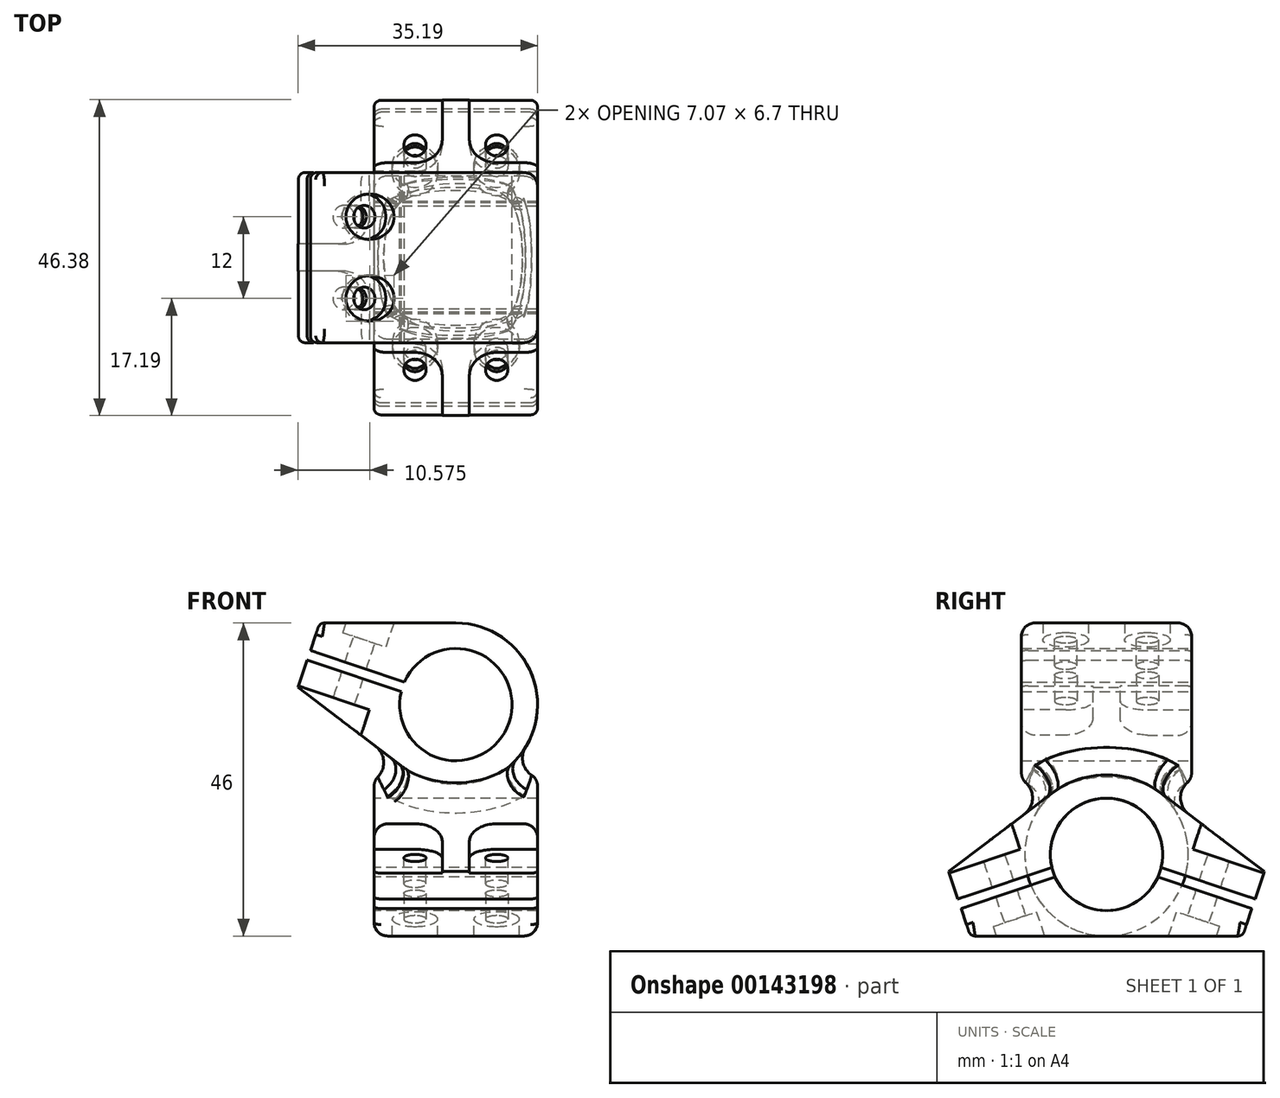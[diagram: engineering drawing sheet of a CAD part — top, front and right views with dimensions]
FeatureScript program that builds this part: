
annotation { "Feature Type Name" : "Feature", "Feature Type Description" : "" }
export const myFeature = defineFeature(function(context is Context, id is Id, definition is map)
    precondition{}
    {
        {
            var Q0;
            Q0=qCreatedBy(makeId("Front.planeOp"),FACE);
            var sketch = newSketch(context, id + "F0", { "sketchPlane" : qUnion([Q0])});
            skCircle(sketch, "E0", {"center": v(0, 11) * mm, "radius": 8.25 * mm});
            skCircle(sketch, "E1", {"center": v(0, 11) * mm, "radius": 12 * mm});
            skSolve(sketch);
        }
        {
            var Q0;
            Q0=qCreatedBy(makeId("Right.planeOp"),FACE);
            var sketch = newSketch(context, id + "F1", { "sketchPlane" : qUnion([Q0])});
            skCircle(sketch, "E2", {"center": v(0, -11) * mm, "radius": 8.25 * mm});
            skCircle(sketch, "E3", {"center": v(0, -11) * mm, "radius": 12 * mm});
            skSolve(sketch);
        }
        {
            var Q0;
            Q0=qSketchRegion(id+"F1",true);
            extrude(context, id + "F2", {"entities" : qUnion([Q0]), "endBound" : BoundingType.SYMMETRIC, "depth" : 24 * mm});
        }
        {
            var Q0;
            Q0=qSketchRegion(id+"F0",true);
            extrude(context, id + "F3", {"entities" : qUnion([Q0]), "operationType" : NewBodyOperationType.ADD, "endBound" : BoundingType.SYMMETRIC, "depth" : 25 * mm});
        }
        {
            var Q0;
            Q0=makeQuery(id+"F3.opExtrude","CAP_FACE",FACE,{"disambiguationData":[OSD([sQuery(id+"F0.wireOp",EDGE,"E0"),sQuery(id+"F0.wireOp",EDGE,"E1")])],"isStart":true});
            var sketch = newSketch(context, id + "F4", { "sketchPlane" : qUnion([Q0])});
            skLineSegment(sketch, "E4", {"start": v(0, 23) * mm, "end": v(20, 23) * mm});
            skLineSegment(sketch, "E5", {"start": v(7.25, 1.44) * mm, "end": v(23.19, 13.52) * mm});
            skLineSegment(sketch, "E6", {"start": v(20, 23) * mm, "end": v(23.19, 13.52) * mm});
            skLineSegment(sketch, "E7", {"start": v(21.6, 18.26) * mm, "end": v(-4.56, 9.47) * mm, "construction": true});
            skSolve(sketch);
        }
        {
            var Q0;
            {var subQ2=sQuery(id+"F4.wireOp",EDGE,"E4");Q0=makeQuery(id+"F4.imprint","IMPRINT",FACE,{"disambiguationData":[TD([[makeQuery(id+"F4.imprint","IMPRINT",EDGE,{"derivedFrom":subQ2}),-1.0]])]});}
            var Q1;
            Q1=makeQuery(id+"F3.opExtrude","CAP_FACE",FACE,{"disambiguationData":[OSD([sQuery(id+"F0.wireOp",EDGE,"E0"),sQuery(id+"F0.wireOp",EDGE,"E1")])],"isStart":false});
            extrude(context, id + "F5", {"entities" : qUnion([Q0]), "operationType" : NewBodyOperationType.ADD, "endBound" : BoundingType.UP_TO_SURFACE, "oppositeDirection" : true, "endBoundEntityFace" : qUnion([Q1]), "depth" : 25 * mm});
        }
        {
            var Q0;
            Q0=makeQuery(id+"F2.opExtrude","CAP_FACE",FACE,{"disambiguationData":[OSD([sQuery(id+"F1.wireOp",EDGE,"E2"),sQuery(id+"F1.wireOp",EDGE,"E3")])],"isStart":false});
            var sketch = newSketch(context, id + "F6", { "sketchPlane" : qUnion([Q0])});
            skLineSegment(sketch, "E8", {"start": v(0, -23) * mm, "end": v(-20, -23) * mm});
            skLineSegment(sketch, "E9", {"start": v(-7.25, -1.44) * mm, "end": v(-23.19, -13.52) * mm});
            skLineSegment(sketch, "E10", {"start": v(-20, -23) * mm, "end": v(-23.19, -13.52) * mm});
            skSolve(sketch);
        }
        {
            var Q0;
            {var subQ2=sQuery(id+"F6.wireOp",EDGE,"E8");Q0=makeQuery(id+"F6.imprint","IMPRINT",FACE,{"disambiguationData":[TD([[makeQuery(id+"F6.imprint","IMPRINT",EDGE,{"derivedFrom":subQ2}),-1.0]])]});}
            var Q1;
            Q1=makeQuery(id+"F2.opExtrude","CAP_FACE",FACE,{"disambiguationData":[OSD([sQuery(id+"F1.wireOp",EDGE,"E2"),sQuery(id+"F1.wireOp",EDGE,"E3")])],"isStart":true});
            extrude(context, id + "F7", {"entities" : qUnion([Q0]), "operationType" : NewBodyOperationType.ADD, "endBound" : BoundingType.UP_TO_SURFACE, "oppositeDirection" : true, "endBoundEntityFace" : qUnion([Q1]), "depth" : 25 * mm});
        }
        {
            var Q0;
            {var subQ0=sQuery(id+"F0.wireOp",EDGE,"E1");Q0=makeQuery(id+"F5.boolean.opBoolean","MERGE",FACE,{"derivedFrom":[makeQuery(id+"F3.opExtrude","CAP_FACE",FACE,{"disambiguationData":[OSD([sQuery(id+"F0.wireOp",EDGE,"E0"),subQ0])],"isStart":true}),makeQuery(id+"F5.opExtrude","CAP_FACE",FACE,{"disambiguationData":[OSD([subQ0,sQuery(id+"F4.wireOp",EDGE,"E4"),sQuery(id+"F4.wireOp",EDGE,"E5"),sQuery(id+"F4.wireOp",EDGE,"E6")])],"isStart":true})]});}
            var sketch = newSketch(context, id + "F8", { "sketchPlane" : qUnion([Q0])});
            skLineSegment(sketch, "E11", {"start": v(21.6, 18.26) * mm, "end": v(-1.1, 10.63) * mm, "construction": true});
            skLineSegment(sketch, "E12", {"start": v(21.35, 18.97) * mm, "end": v(2.27, 12.55) * mm});
            skLineSegment(sketch, "E13", {"start": v(2.27, 12.55) * mm, "end": v(2.74, 11.13) * mm});
            skLineSegment(sketch, "E14", {"start": v(2.74, 11.13) * mm, "end": v(21.83, 17.55) * mm});
            skLineSegment(sketch, "E15", {"start": v(21.83, 17.55) * mm, "end": v(21.35, 18.97) * mm});
            skSolve(sketch);
        }
        {
            var Q0;
            Q0=qSketchRegion(id+"F8",true);
            extrude(context, id + "F9", {"entities" : qUnion([Q0]), "operationType" : NewBodyOperationType.REMOVE, "endBound" : BoundingType.UP_TO_NEXT, "oppositeDirection" : true, "depth" : 25 * mm});
        }
        {
            var Q0;
            {var subQ0=sQuery(id+"F1.wireOp",EDGE,"E3");Q0=makeQuery(id+"F7.boolean.opBoolean","MERGE",FACE,{"derivedFrom":[makeQuery(id+"F2.opExtrude","CAP_FACE",FACE,{"disambiguationData":[OSD([sQuery(id+"F1.wireOp",EDGE,"E2"),subQ0])],"isStart":true}),makeQuery(id+"F7.opExtrude","CAP_FACE",FACE,{"disambiguationData":[OSD([subQ0,sQuery(id+"F6.wireOp",EDGE,"E8"),sQuery(id+"F6.wireOp",EDGE,"E9"),sQuery(id+"F6.wireOp",EDGE,"E10")])],"isStart":false})]});}
            var sketch = newSketch(context, id + "F10", { "sketchPlane" : qUnion([Q0])});
            skLineSegment(sketch, "E16", {"start": v(21.6, -18.26) * mm, "end": v(-2.55, -10.14) * mm, "construction": true});
            skLineSegment(sketch, "E17", {"start": v(21.83, -17.55) * mm, "end": v(1.3, -10.65) * mm});
            skLineSegment(sketch, "E18", {"start": v(1.3, -10.65) * mm, "end": v(0.83, -12.07) * mm});
            skLineSegment(sketch, "E19", {"start": v(0.83, -12.07) * mm, "end": v(21.35, -18.97) * mm});
            skLineSegment(sketch, "E20", {"start": v(21.35, -18.97) * mm, "end": v(21.83, -17.55) * mm});
            skSolve(sketch);
        }
        {
            var Q0;
            Q0=qSketchRegion(id+"F10",true);
            extrude(context, id + "F11", {"entities" : qUnion([Q0]), "operationType" : NewBodyOperationType.REMOVE, "endBound" : BoundingType.UP_TO_NEXT, "oppositeDirection" : true, "depth" : 25 * mm});
        }
        {
            var Q0;
            Q0=makeQuery(id+"F9.boolean.opBoolean","COPY",FACE,{"derivedFrom":makeQuery(id+"F9.opExtrude","SWEPT_FACE",FACE,{"disambiguationData":[OSD([sQuery(id+"F8.wireOp",EDGE,"E12")])]})});
            cPlane(context, id + "F12", {"entities" : qUnion([Q0]), "cplaneType" : CPlaneType.OFFSET, "offset" : 4 * mm, "oppositeDirection" : true, "width" : 150 * mm, "height" : 150 * mm});
        }
        {
            var Q0;
            Q0=qCreatedBy(id+"F12.planeOp",FACE);
            var sketch = newSketch(context, id + "F13", { "sketchPlane" : qUnion([Q0])});
            skCircle(sketch, "E21", {"center": v(-19.29, 6) * mm, "radius": 3.35 * mm});
            skCircle(sketch, "E22.MirrorC", {"center": v(-19.29, -6) * mm, "radius": 3.35 * mm});
            skSolve(sketch);
        }
        {
            var Q0;
            Q0=qSketchRegion(id+"F13",true);
            extrude(context, id + "F14", {"entities" : qUnion([Q0]), "operationType" : NewBodyOperationType.REMOVE, "endBound" : BoundingType.UP_TO_NEXT, "oppositeDirection" : true, "depth" : 25 * mm});
        }
        {
            var Q0;
            Q0=qCreatedBy(id+"F12.planeOp",FACE);
            var sketch = newSketch(context, id + "F15", { "sketchPlane" : qUnion([Q0])});
            skCircle(sketch, "E23", {"center": v(-19.29, 6) * mm, "radius": 1.65 * mm});
            skCircle(sketch, "E24.MirrorC", {"center": v(-19.29, -6) * mm, "radius": 1.65 * mm});
            skSolve(sketch);
        }
        {
            var Q0;
            Q0=qSketchRegion(id+"F15",true);
            extrude(context, id + "F16", {"entities" : qUnion([Q0]), "operationType" : NewBodyOperationType.REMOVE, "endBound" : BoundingType.UP_TO_NEXT, "depth" : 25 * mm});
        }
        {
            var Q0;
            Q0=makeQuery(id+"F9.boolean.opBoolean","COPY",FACE,{"derivedFrom":makeQuery(id+"F9.opExtrude","SWEPT_FACE",FACE,{"disambiguationData":[OSD([sQuery(id+"F8.wireOp",EDGE,"E14")])]})});
            cPlane(context, id + "F17", {"entities" : qUnion([Q0]), "cplaneType" : CPlaneType.OFFSET, "offset" : 4 * mm, "oppositeDirection" : true, "width" : 150 * mm, "height" : 150 * mm});
        }
        {
            var Q0;
            Q0=qCreatedBy(id+"F17.planeOp",FACE);
            var sketch = newSketch(context, id + "F18", { "sketchPlane" : qUnion([Q0])});
            skCircle(sketch, "E25", {"center": v(-19.29, 6) * mm, "radius": 1.65 * mm});
            skCircle(sketch, "E26.MirrorC", {"center": v(-19.29, -6) * mm, "radius": 1.65 * mm});
            skSolve(sketch);
        }
        {
            var Q0;
            Q0=qSketchRegion(id+"F18",true);
            extrude(context, id + "F19", {"entities" : qUnion([Q0]), "operationType" : NewBodyOperationType.REMOVE, "endBound" : BoundingType.UP_TO_NEXT, "depth" : 25 * mm});
        }
        {
            var Q0;
            Q0=qCreatedBy(id+"F17.planeOp",FACE);
            var sketch = newSketch(context, id + "F20", { "sketchPlane" : qUnion([Q0])});
            skArc(sketch, "E27", {"start": v(-15.29, -6) * mm, "mid": v(-16.46, -3.17) * mm, "end": v(-19.29, -2) * mm});
            skLineSegment(sketch, "E28", {"start": v(-15.29, -6) * mm, "end": v(-15.29, -12.5) * mm});
            skLineSegment(sketch, "E29", {"start": v(-19.29, -2) * mm, "end": v(-26.29, -2) * mm});
            skLineSegment(sketch, "E30", {"start": v(-15.29, -12.5) * mm, "end": v(-26.29, -12.5) * mm});
            skLineSegment(sketch, "E31", {"start": v(-26.29, -12.5) * mm, "end": v(-26.29, -2) * mm});
            skLineSegment(sketch, "E32.MirrorCS", {"start": v(-15.29, 6) * mm, "end": v(-15.29, 12.5) * mm});
            skArc(sketch, "E33.MirrorCS", {"start": v(-15.29, 6) * mm, "mid": v(-16.46, 3.17) * mm, "end": v(-19.29, 2) * mm});
            skLineSegment(sketch, "E34.MirrorCS", {"start": v(-19.29, 2) * mm, "end": v(-26.29, 2) * mm});
            skLineSegment(sketch, "E35.MirrorCS", {"start": v(-15.29, 12.5) * mm, "end": v(-26.29, 12.5) * mm});
            skLineSegment(sketch, "E36.MirrorCS", {"start": v(-26.29, 12.5) * mm, "end": v(-26.29, 2) * mm});
            skSolve(sketch);
        }
        {
            var Q0;
            Q0=qSketchRegion(id+"F20",true);
            extrude(context, id + "F21", {"entities" : qUnion([Q0]), "operationType" : NewBodyOperationType.REMOVE, "endBound" : BoundingType.UP_TO_NEXT, "oppositeDirection" : true, "depth" : 25 * mm});
        }
        {
            var Q0;
            Q0=makeQuery(id+"F11.boolean.opBoolean","COPY",FACE,{"derivedFrom":makeQuery(id+"F11.opExtrude","SWEPT_FACE",FACE,{"disambiguationData":[OSD([sQuery(id+"F10.wireOp",EDGE,"E19")])]})});
            cPlane(context, id + "F22", {"entities" : qUnion([Q0]), "cplaneType" : CPlaneType.OFFSET, "offset" : 4 * mm, "oppositeDirection" : true, "width" : 150 * mm, "height" : 150 * mm});
        }
        {
            var Q0;
            Q0=qCreatedBy(id+"F22.planeOp",FACE);
            var sketch = newSketch(context, id + "F23", { "sketchPlane" : qUnion([Q0])});
            skCircle(sketch, "E37", {"center": v(6, -19.29) * mm, "radius": 1.65 * mm});
            skCircle(sketch, "E38.MirrorC", {"center": v(-6, -19.29) * mm, "radius": 1.65 * mm});
            skSolve(sketch);
        }
        {
            var Q0;
            Q0=qSketchRegion(id+"F23",true);
            extrude(context, id + "F24", {"entities" : qUnion([Q0]), "operationType" : NewBodyOperationType.REMOVE, "endBound" : BoundingType.UP_TO_NEXT, "depth" : 25 * mm});
        }
        {
            var Q0;
            Q0=qCreatedBy(id+"F22.planeOp",FACE);
            var sketch = newSketch(context, id + "F25", { "sketchPlane" : qUnion([Q0])});
            skCircle(sketch, "E39", {"center": v(6, -19.29) * mm, "radius": 3.35 * mm});
            skCircle(sketch, "E40.MirrorC", {"center": v(-6, -19.29) * mm, "radius": 3.35 * mm});
            skSolve(sketch);
        }
        {
            var Q0;
            Q0=qSketchRegion(id+"F25",true);
            extrude(context, id + "F26", {"entities" : qUnion([Q0]), "operationType" : NewBodyOperationType.REMOVE, "endBound" : BoundingType.UP_TO_NEXT, "oppositeDirection" : true, "depth" : 25 * mm});
        }
        {
            var Q0;
            Q0=makeQuery(id+"F11.boolean.opBoolean","COPY",FACE,{"derivedFrom":makeQuery(id+"F11.opExtrude","SWEPT_FACE",FACE,{"disambiguationData":[OSD([sQuery(id+"F10.wireOp",EDGE,"E17")])]})});
            cPlane(context, id + "F27", {"entities" : qUnion([Q0]), "cplaneType" : CPlaneType.OFFSET, "offset" : 4 * mm, "oppositeDirection" : true, "width" : 150 * mm, "height" : 150 * mm});
        }
        {
            var Q0;
            Q0=qCreatedBy(id+"F27.planeOp",FACE);
            var sketch = newSketch(context, id + "F28", { "sketchPlane" : qUnion([Q0])});
            skCircle(sketch, "E41", {"center": v(6, 19.29) * mm, "radius": 1.65 * mm});
            skCircle(sketch, "E42.MirrorC", {"center": v(-6, 19.29) * mm, "radius": 1.65 * mm});
            skSolve(sketch);
        }
        {
            var Q0;
            Q0=qSketchRegion(id+"F28",true);
            extrude(context, id + "F29", {"entities" : qUnion([Q0]), "operationType" : NewBodyOperationType.REMOVE, "endBound" : BoundingType.UP_TO_NEXT, "depth" : 25 * mm});
        }
        {
            var Q0;
            Q0=qCreatedBy(id+"F27.planeOp",FACE);
            var sketch = newSketch(context, id + "F30", { "sketchPlane" : qUnion([Q0])});
            skArc(sketch, "E43", {"start": v(-6, 15.29) * mm, "mid": v(-3.17, 16.46) * mm, "end": v(-2, 19.29) * mm});
            skLineSegment(sketch, "E44", {"start": v(-6, 15.29) * mm, "end": v(-12, 15.29) * mm});
            skLineSegment(sketch, "E45", {"start": v(-2, 19.29) * mm, "end": v(-2, 26.29) * mm});
            skLineSegment(sketch, "E46", {"start": v(-12, 15.29) * mm, "end": v(-12, 26.29) * mm});
            skLineSegment(sketch, "E47", {"start": v(-12, 26.29) * mm, "end": v(-2, 26.29) * mm});
            skLineSegment(sketch, "E48.MirrorCS", {"start": v(6, 15.29) * mm, "end": v(12, 15.29) * mm});
            skArc(sketch, "E49.MirrorCS", {"start": v(6, 15.29) * mm, "mid": v(3.17, 16.46) * mm, "end": v(2, 19.29) * mm});
            skLineSegment(sketch, "E50.MirrorCS", {"start": v(2, 19.29) * mm, "end": v(2, 26.29) * mm});
            skLineSegment(sketch, "E51.MirrorCS", {"start": v(12, 15.29) * mm, "end": v(12, 26.29) * mm});
            skLineSegment(sketch, "E52.MirrorCS", {"start": v(12, 26.29) * mm, "end": v(2, 26.29) * mm});
            skSolve(sketch);
        }
        {
            var Q0;
            Q0=qSketchRegion(id+"F30",true);
            extrude(context, id + "F31", {"entities" : qUnion([Q0]), "operationType" : NewBodyOperationType.REMOVE, "endBound" : BoundingType.UP_TO_NEXT, "oppositeDirection" : true, "depth" : 25 * mm});
        }
        {
            var Q0;
            {var subQ0=sQuery(id+"F4.wireOp",EDGE,"E6");var subQ1=sQuery(id+"F4.wireOp",EDGE,"E4");Q0=makeQuery(id+"F9.boolean.opBoolean","SPLIT",EDGE,{"disambiguationData":[TD([makeQuery(id+"F5.opExtrude","SWEPT_FACE",FACE,{"disambiguationData":[OSD([subQ1])]})])],"derivedFrom":makeQuery(id+"F5.opExtrude","CAP_EDGE",EDGE,{"disambiguationData":[OSD([subQ0])],"isStart":false})});}
            var Q1;
            Q1=makeQuery(id+"F5.opExtrude","SWEPT_EDGE",EDGE,{"disambiguationData":[OSD([sQuery(id+"F4.wireOp",EDGE,"E4"),sQuery(id+"F4.wireOp",EDGE,"E6")])]});
            var Q2;
            Q2=makeQuery(id+"F21.boolean.opBoolean","COPY",EDGE,{"derivedFrom":makeQuery(id+"F21.opExtrude","SWEPT_EDGE",EDGE,{"disambiguationData":[OSD([sQuery(id+"F20.wireOp",EDGE,"E28"),sQuery(id+"F20.wireOp",EDGE,"E30")])]})});
            var Q3;
            Q3=makeQuery(id+"F21.boolean.opBoolean","COPY",EDGE,{"derivedFrom":makeQuery(id+"F21.opExtrude","CAP_EDGE",EDGE,{"disambiguationData":[OSD([sQuery(id+"F20.wireOp",EDGE,"E30")])],"isStart":true})});
            var Q4;
            Q4=makeQuery(id+"F21.boolean.opBoolean","COPY",EDGE,{"derivedFrom":makeQuery(id+"F21.opExtrude","SWEPT_EDGE",EDGE,{"disambiguationData":[OSD([sQuery(id+"F20.wireOp",EDGE,"E32.MirrorCS"),sQuery(id+"F20.wireOp",EDGE,"E35.MirrorCS")])]})});
            var Q5;
            Q5=makeQuery(id+"F21.boolean.opBoolean","COPY",EDGE,{"derivedFrom":makeQuery(id+"F21.opExtrude","CAP_EDGE",EDGE,{"disambiguationData":[OSD([sQuery(id+"F20.wireOp",EDGE,"E35.MirrorCS")])],"isStart":true})});
            var Q6;
            {var subQ0=sQuery(id+"F4.wireOp",EDGE,"E6");var subQ1=sQuery(id+"F4.wireOp",EDGE,"E5");Q6=makeQuery(id+"F9.boolean.opBoolean","SPLIT",EDGE,{"disambiguationData":[TD([makeQuery(id+"F5.opExtrude","SWEPT_FACE",FACE,{"disambiguationData":[OSD([subQ1])]})])],"derivedFrom":makeQuery(id+"F5.opExtrude","CAP_EDGE",EDGE,{"disambiguationData":[OSD([subQ0])],"isStart":true})});}
            var Q7;
            {var subQ0=sQuery(id+"F4.wireOp",EDGE,"E6");var subQ1=sQuery(id+"F4.wireOp",EDGE,"E4");Q7=makeQuery(id+"F9.boolean.opBoolean","SPLIT",EDGE,{"disambiguationData":[TD([makeQuery(id+"F5.opExtrude","SWEPT_FACE",FACE,{"disambiguationData":[OSD([subQ1])]})])],"derivedFrom":makeQuery(id+"F5.opExtrude","CAP_EDGE",EDGE,{"disambiguationData":[OSD([subQ0])],"isStart":true})});}
            var Q8;
            {var subQ0=sQuery(id+"F4.wireOp",EDGE,"E6");var subQ1=sQuery(id+"F4.wireOp",EDGE,"E5");Q8=makeQuery(id+"F9.boolean.opBoolean","SPLIT",EDGE,{"disambiguationData":[TD([makeQuery(id+"F5.opExtrude","SWEPT_FACE",FACE,{"disambiguationData":[OSD([subQ1])]})])],"derivedFrom":makeQuery(id+"F5.opExtrude","CAP_EDGE",EDGE,{"disambiguationData":[OSD([subQ0])],"isStart":false})});}
            var Q9;
            Q9=makeQuery(id+"F21.boolean.opBoolean","COPY",EDGE,{"derivedFrom":makeQuery(id+"F21.opExtrude","CAP_EDGE",EDGE,{"disambiguationData":[OSD([sQuery(id+"F20.wireOp",EDGE,"E31")])],"isStart":true})});
            var Q10;
            Q10=makeQuery(id+"F21.boolean.opBoolean","COPY",EDGE,{"derivedFrom":makeQuery(id+"F21.opExtrude","CAP_EDGE",EDGE,{"disambiguationData":[OSD([sQuery(id+"F20.wireOp",EDGE,"E36.MirrorCS")])],"isStart":true})});
            var Q11;
            {var subQ0=sQuery(id+"F6.wireOp",EDGE,"E10");var subQ1=sQuery(id+"F6.wireOp",EDGE,"E8");Q11=makeQuery(id+"F11.boolean.opBoolean","SPLIT",EDGE,{"disambiguationData":[TD([makeQuery(id+"F7.opExtrude","SWEPT_FACE",FACE,{"disambiguationData":[OSD([subQ1])]})])],"derivedFrom":makeQuery(id+"F7.opExtrude","CAP_EDGE",EDGE,{"disambiguationData":[OSD([subQ0])],"isStart":false})});}
            var Q12;
            Q12=makeQuery(id+"F7.opExtrude","SWEPT_EDGE",EDGE,{"disambiguationData":[OSD([sQuery(id+"F6.wireOp",EDGE,"E8"),sQuery(id+"F6.wireOp",EDGE,"E10")])]});
            var Q13;
            {var subQ0=sQuery(id+"F6.wireOp",EDGE,"E10");var subQ1=sQuery(id+"F6.wireOp",EDGE,"E8");Q13=makeQuery(id+"F11.boolean.opBoolean","SPLIT",EDGE,{"disambiguationData":[TD([makeQuery(id+"F7.opExtrude","SWEPT_FACE",FACE,{"disambiguationData":[OSD([subQ1])]})])],"derivedFrom":makeQuery(id+"F7.opExtrude","CAP_EDGE",EDGE,{"disambiguationData":[OSD([subQ0])],"isStart":true})});}
            var Q14;
            {var subQ0=sQuery(id+"F6.wireOp",EDGE,"E10");var subQ1=sQuery(id+"F6.wireOp",EDGE,"E9");Q14=makeQuery(id+"F11.boolean.opBoolean","SPLIT",EDGE,{"disambiguationData":[TD([makeQuery(id+"F7.opExtrude","SWEPT_FACE",FACE,{"disambiguationData":[OSD([subQ1])]})])],"derivedFrom":makeQuery(id+"F7.opExtrude","CAP_EDGE",EDGE,{"disambiguationData":[OSD([subQ0])],"isStart":true})});}
            var Q15;
            {var subQ0=sQuery(id+"F6.wireOp",EDGE,"E10");var subQ1=sQuery(id+"F6.wireOp",EDGE,"E9");Q15=makeQuery(id+"F11.boolean.opBoolean","SPLIT",EDGE,{"disambiguationData":[TD([makeQuery(id+"F7.opExtrude","SWEPT_FACE",FACE,{"disambiguationData":[OSD([subQ1])]})])],"derivedFrom":makeQuery(id+"F7.opExtrude","CAP_EDGE",EDGE,{"disambiguationData":[OSD([subQ0])],"isStart":false})});}
            var Q16;
            Q16=makeQuery(id+"F31.boolean.opBoolean","COPY",EDGE,{"derivedFrom":makeQuery(id+"F31.opExtrude","CAP_EDGE",EDGE,{"disambiguationData":[OSD([sQuery(id+"F30.wireOp",EDGE,"E46")])],"isStart":true})});
            var Q17;
            Q17=makeQuery(id+"F31.boolean.opBoolean","COPY",EDGE,{"derivedFrom":makeQuery(id+"F31.opExtrude","SWEPT_EDGE",EDGE,{"disambiguationData":[OSD([sQuery(id+"F30.wireOp",EDGE,"E44"),sQuery(id+"F30.wireOp",EDGE,"E46")])]})});
            var Q18;
            Q18=makeQuery(id+"F31.boolean.opBoolean","COPY",EDGE,{"derivedFrom":makeQuery(id+"F31.opExtrude","CAP_EDGE",EDGE,{"disambiguationData":[OSD([sQuery(id+"F30.wireOp",EDGE,"E47")])],"isStart":true})});
            var Q19;
            Q19=makeQuery(id+"F31.boolean.opBoolean","COPY",EDGE,{"derivedFrom":makeQuery(id+"F31.opExtrude","CAP_EDGE",EDGE,{"disambiguationData":[OSD([sQuery(id+"F30.wireOp",EDGE,"E52.MirrorCS")])],"isStart":true})});
            var Q20;
            Q20=makeQuery(id+"F31.boolean.opBoolean","COPY",EDGE,{"derivedFrom":makeQuery(id+"F31.opExtrude","CAP_EDGE",EDGE,{"disambiguationData":[OSD([sQuery(id+"F30.wireOp",EDGE,"E51.MirrorCS")])],"isStart":true})});
            var Q21;
            Q21=makeQuery(id+"F31.boolean.opBoolean","COPY",EDGE,{"derivedFrom":makeQuery(id+"F31.opExtrude","SWEPT_EDGE",EDGE,{"disambiguationData":[OSD([sQuery(id+"F30.wireOp",EDGE,"E48.MirrorCS"),sQuery(id+"F30.wireOp",EDGE,"E51.MirrorCS")])]})});
            var Q22;
            {var subQ0=sQuery(id+"F1.wireOp",EDGE,"E3");Q22=makeQuery(id+"Fq04dk8cSvX2TGJ_1.opFillet","BLEND_EDGE",EDGE,{"blendedFrom":[makeQuery(id+"F3.boolean.opBoolean","INTERSECT",EDGE,{"derivedFrom":[makeQuery(id+"F2.opExtrude","SWEPT_FACE",FACE,{"disambiguationData":[OSD([subQ0])]}),makeQuery(id+"F3.opExtrude","SWEPT_FACE",FACE,{"disambiguationData":[OSD([sQuery(id+"F0.wireOp",EDGE,"E1")])]})]}),makeQuery(id+"F2.opExtrude","CAP_FACE",FACE,{"disambiguationData":[OSD([sQuery(id+"F1.wireOp",EDGE,"E2"),subQ0])],"isStart":true})],"blendedInto":[makeQuery(id+"F2.opExtrude","CAP_FACE",FACE,{"disambiguationData":[OSD([sQuery(id+"F1.wireOp",EDGE,"E2"),subQ0])],"isStart":true})]});}
            var Q23;
            {var subQ0=sQuery(id+"F1.wireOp",EDGE,"E3");Q23=makeQuery(id+"Fq04dk8cSvX2TGJ_1.opFillet","BLEND_EDGE",EDGE,{"blendedFrom":[makeQuery(id+"F3.boolean.opBoolean","INTERSECT",EDGE,{"derivedFrom":[makeQuery(id+"F2.opExtrude","SWEPT_FACE",FACE,{"disambiguationData":[OSD([subQ0])]}),makeQuery(id+"F3.opExtrude","SWEPT_FACE",FACE,{"disambiguationData":[OSD([sQuery(id+"F0.wireOp",EDGE,"E1")])]})]}),makeQuery(id+"F2.opExtrude","CAP_FACE",FACE,{"disambiguationData":[OSD([sQuery(id+"F1.wireOp",EDGE,"E2"),subQ0])],"isStart":false})],"blendedInto":[makeQuery(id+"F2.opExtrude","CAP_FACE",FACE,{"disambiguationData":[OSD([sQuery(id+"F1.wireOp",EDGE,"E2"),subQ0])],"isStart":false})]});}
            var Q24;
            Q24=makeQuery(id+"F26.boolean.opBoolean","COPY",EDGE,{"derivedFrom":makeQuery(id+"F26.opExtrude","CAP_EDGE",EDGE,{"disambiguationData":[OSD([sQuery(id+"F25.wireOp",EDGE,"E40.MirrorC")])],"isStart":false})});
            var Q25;
            Q25=makeQuery(id+"F26.boolean.opBoolean","COPY",EDGE,{"derivedFrom":makeQuery(id+"F26.opExtrude","CAP_EDGE",EDGE,{"disambiguationData":[OSD([sQuery(id+"F25.wireOp",EDGE,"E39")])],"isStart":false})});
            var Q26;
            Q26=makeQuery(id+"F14.boolean.opBoolean","COPY",EDGE,{"derivedFrom":makeQuery(id+"F14.opExtrude","CAP_EDGE",EDGE,{"disambiguationData":[OSD([sQuery(id+"F13.wireOp",EDGE,"E22.MirrorC")])],"isStart":false})});
            var Q27;
            Q27=makeQuery(id+"F14.boolean.opBoolean","COPY",EDGE,{"derivedFrom":makeQuery(id+"F14.opExtrude","CAP_EDGE",EDGE,{"disambiguationData":[OSD([sQuery(id+"F13.wireOp",EDGE,"E21")])],"isStart":false})});
            fillet(context, id + "F32", {"entities" : qUnion([Q0, Q1, Q2, Q3, Q4, Q5, Q6, Q7, Q8, Q9, Q10, Q11, Q12, Q13, Q14, Q15, Q16, Q17, Q18, Q19, Q20, Q21, Q22, Q23, Q24, Q25, Q26, Q27]), "radius" : 1 * mm, "tangentPropagation" : true, "allowEdgeOverflow" : false});
        }
        {
            var Q0;
            {var subQ0=sQuery(id+"F6.wireOp",EDGE,"E10");var subQ1=sQuery(id+"F6.wireOp",EDGE,"E8");Q0=makeQuery(id+"F32.opFillet","BLEND_EDGE",EDGE,{"blendedFrom":[makeQuery(id+"F7.opExtrude","SWEPT_EDGE",EDGE,{"disambiguationData":[OSD([subQ1,subQ0])]}),makeQuery(id+"F11.boolean.opBoolean","SPLIT",EDGE,{"disambiguationData":[TD([makeQuery(id+"F7.opExtrude","SWEPT_FACE",FACE,{"disambiguationData":[OSD([subQ1])]})])],"derivedFrom":makeQuery(id+"F7.opExtrude","CAP_EDGE",EDGE,{"disambiguationData":[OSD([subQ0])],"isStart":false})})],"blendedInto":[]});}
            var Q1;
            {var subQ0=sQuery(id+"F6.wireOp",EDGE,"E8");var subQ1=makeQuery(id+"F7.opExtrude","SWEPT_FACE",FACE,{"disambiguationData":[OSD([subQ0])]});var subQ2=sQuery(id+"F6.wireOp",EDGE,"E10");Q1=makeQuery(id+"F32.opFillet","BLEND_EDGE",EDGE,{"blendedFrom":[makeQuery(id+"F11.boolean.opBoolean","SPLIT",EDGE,{"disambiguationData":[TD([subQ1])],"derivedFrom":makeQuery(id+"F7.opExtrude","CAP_EDGE",EDGE,{"disambiguationData":[OSD([subQ2])],"isStart":false})}),subQ1],"blendedInto":[subQ1]});}
            var Q2;
            Q2=makeQuery(id+"F7.opExtrude","CAP_EDGE",EDGE,{"disambiguationData":[OSD([sQuery(id+"F6.wireOp",EDGE,"E8")])],"isStart":false});
            var Q3;
            Q3=makeQuery(id+"F2.opExtrude","CAP_EDGE",EDGE,{"disambiguationData":[OSD([sQuery(id+"F1.wireOp",EDGE,"E3")])],"isStart":true});
            var Q4;
            {var subQ0=sQuery(id+"F1.wireOp",EDGE,"E3");Q4=makeQuery(id+"Fq04dk8cSvX2TGJ_1.opFillet","BLEND_EDGE",EDGE,{"blendedFrom":[makeQuery(id+"F3.boolean.opBoolean","INTERSECT",EDGE,{"derivedFrom":[makeQuery(id+"F2.opExtrude","SWEPT_FACE",FACE,{"disambiguationData":[OSD([subQ0])]}),makeQuery(id+"F3.opExtrude","SWEPT_FACE",FACE,{"disambiguationData":[OSD([sQuery(id+"F0.wireOp",EDGE,"E1")])]})]}),makeQuery(id+"F2.opExtrude","CAP_FACE",FACE,{"disambiguationData":[OSD([sQuery(id+"F1.wireOp",EDGE,"E2"),subQ0])],"isStart":true})],"blendedInto":[makeQuery(id+"F2.opExtrude","CAP_FACE",FACE,{"disambiguationData":[OSD([sQuery(id+"F1.wireOp",EDGE,"E2"),subQ0])],"isStart":true})]});}
            var Q5;
            {var subQ0=sQuery(id+"F1.wireOp",EDGE,"E3");Q5=makeQuery(id+"Fq04dk8cSvX2TGJ_1.opFillet","BLEND_EDGE",EDGE,{"blendedFrom":[makeQuery(id+"F3.boolean.opBoolean","INTERSECT",EDGE,{"derivedFrom":[makeQuery(id+"F2.opExtrude","SWEPT_FACE",FACE,{"disambiguationData":[OSD([subQ0])]}),makeQuery(id+"F3.opExtrude","SWEPT_FACE",FACE,{"disambiguationData":[OSD([sQuery(id+"F0.wireOp",EDGE,"E1")])]})]}),makeQuery(id+"F2.opExtrude","CAP_FACE",FACE,{"disambiguationData":[OSD([sQuery(id+"F1.wireOp",EDGE,"E2"),subQ0])],"isStart":true})],"blendedInto":[makeQuery(id+"F2.opExtrude","CAP_FACE",FACE,{"disambiguationData":[OSD([sQuery(id+"F1.wireOp",EDGE,"E2"),subQ0])],"isStart":true})]});}
            var Q6;
            Q6=makeQuery(id+"F2.opExtrude","CAP_EDGE",EDGE,{"disambiguationData":[OSD([sQuery(id+"F1.wireOp",EDGE,"E3")])],"isStart":true});
            var Q7;
            Q7=makeQuery(id+"F7.opExtrude","CAP_EDGE",EDGE,{"disambiguationData":[OSD([sQuery(id+"F6.wireOp",EDGE,"E9")])],"isStart":false});
            var Q8;
            Q8=makeQuery(id+"F32.opFillet","BLEND_EDGE",EDGE,{"blendedFrom":[makeQuery(id+"F31.boolean.opBoolean","COPY",EDGE,{"derivedFrom":makeQuery(id+"F31.opExtrude","SWEPT_EDGE",EDGE,{"disambiguationData":[OSD([sQuery(id+"F30.wireOp",EDGE,"E44"),sQuery(id+"F30.wireOp",EDGE,"E46")])]})}),makeQuery(id+"F7.opExtrude","SWEPT_FACE",FACE,{"disambiguationData":[OSD([sQuery(id+"F6.wireOp",EDGE,"E9")])]})],"blendedInto":[makeQuery(id+"F7.opExtrude","SWEPT_FACE",FACE,{"disambiguationData":[OSD([sQuery(id+"F6.wireOp",EDGE,"E9")])]})]});
            var Q9;
            Q9=makeQuery(id+"F7.opExtrude","CAP_EDGE",EDGE,{"disambiguationData":[OSD([sQuery(id+"F6.wireOp",EDGE,"E8")])],"isStart":true});
            var Q10;
            {var subQ0=sQuery(id+"F6.wireOp",EDGE,"E10");var subQ1=sQuery(id+"F6.wireOp",EDGE,"E8");Q10=makeQuery(id+"F32.opFillet","BLEND_EDGE",EDGE,{"blendedFrom":[makeQuery(id+"F7.opExtrude","SWEPT_EDGE",EDGE,{"disambiguationData":[OSD([subQ1,subQ0])]}),makeQuery(id+"F11.boolean.opBoolean","SPLIT",EDGE,{"disambiguationData":[TD([makeQuery(id+"F7.opExtrude","SWEPT_FACE",FACE,{"disambiguationData":[OSD([subQ1])]})])],"derivedFrom":makeQuery(id+"F7.opExtrude","CAP_EDGE",EDGE,{"disambiguationData":[OSD([subQ0])],"isStart":true})})],"blendedInto":[]});}
            var Q11;
            {var subQ0=sQuery(id+"F6.wireOp",EDGE,"E8");var subQ1=makeQuery(id+"F7.opExtrude","SWEPT_FACE",FACE,{"disambiguationData":[OSD([subQ0])]});var subQ2=sQuery(id+"F6.wireOp",EDGE,"E10");Q11=makeQuery(id+"F32.opFillet","BLEND_EDGE",EDGE,{"blendedFrom":[makeQuery(id+"F11.boolean.opBoolean","SPLIT",EDGE,{"disambiguationData":[TD([subQ1])],"derivedFrom":makeQuery(id+"F7.opExtrude","CAP_EDGE",EDGE,{"disambiguationData":[OSD([subQ2])],"isStart":true})}),subQ1],"blendedInto":[subQ1]});}
            var Q12;
            Q12=makeQuery(id+"F2.opExtrude","CAP_EDGE",EDGE,{"disambiguationData":[OSD([sQuery(id+"F1.wireOp",EDGE,"E3")])],"isStart":false});
            var Q13;
            Q13=makeQuery(id+"F7.opExtrude","CAP_EDGE",EDGE,{"disambiguationData":[OSD([sQuery(id+"F6.wireOp",EDGE,"E9")])],"isStart":true});
            var Q14;
            Q14=makeQuery(id+"F32.opFillet","BLEND_EDGE",EDGE,{"blendedFrom":[makeQuery(id+"F31.boolean.opBoolean","COPY",EDGE,{"derivedFrom":makeQuery(id+"F31.opExtrude","SWEPT_EDGE",EDGE,{"disambiguationData":[OSD([sQuery(id+"F30.wireOp",EDGE,"E48.MirrorCS"),sQuery(id+"F30.wireOp",EDGE,"E51.MirrorCS")])]})}),makeQuery(id+"F7.opExtrude","SWEPT_FACE",FACE,{"disambiguationData":[OSD([sQuery(id+"F6.wireOp",EDGE,"E9")])]})],"blendedInto":[makeQuery(id+"F7.opExtrude","SWEPT_FACE",FACE,{"disambiguationData":[OSD([sQuery(id+"F6.wireOp",EDGE,"E9")])]})]});
            var Q15;
            {var subQ0=sQuery(id+"F4.wireOp",EDGE,"E6");var subQ1=sQuery(id+"F4.wireOp",EDGE,"E4");Q15=makeQuery(id+"F32.opFillet","BLEND_EDGE",EDGE,{"blendedFrom":[makeQuery(id+"F5.opExtrude","SWEPT_EDGE",EDGE,{"disambiguationData":[OSD([subQ1,subQ0])]}),makeQuery(id+"F9.boolean.opBoolean","SPLIT",EDGE,{"disambiguationData":[TD([makeQuery(id+"F5.opExtrude","SWEPT_FACE",FACE,{"disambiguationData":[OSD([subQ1])]})])],"derivedFrom":makeQuery(id+"F5.opExtrude","CAP_EDGE",EDGE,{"disambiguationData":[OSD([subQ0])],"isStart":true})})],"blendedInto":[]});}
            var Q16;
            Q16=makeQuery(id+"F5.opExtrude","CAP_EDGE",EDGE,{"disambiguationData":[OSD([sQuery(id+"F4.wireOp",EDGE,"E4")])],"isStart":true});
            var Q17;
            {var subQ0=sQuery(id+"F4.wireOp",EDGE,"E4");var subQ1=makeQuery(id+"F5.opExtrude","SWEPT_FACE",FACE,{"disambiguationData":[OSD([subQ0])]});var subQ2=sQuery(id+"F4.wireOp",EDGE,"E6");Q17=makeQuery(id+"F32.opFillet","BLEND_EDGE",EDGE,{"blendedFrom":[makeQuery(id+"F9.boolean.opBoolean","SPLIT",EDGE,{"disambiguationData":[TD([subQ1])],"derivedFrom":makeQuery(id+"F5.opExtrude","CAP_EDGE",EDGE,{"disambiguationData":[OSD([subQ2])],"isStart":true})}),subQ1],"blendedInto":[subQ1]});}
            var Q18;
            Q18=makeQuery(id+"F3.opExtrude","CAP_EDGE",EDGE,{"disambiguationData":[OSD([sQuery(id+"F0.wireOp",EDGE,"E1")])],"isStart":true});
            var Q19;
            Q19=makeQuery(id+"F5.opExtrude","CAP_EDGE",EDGE,{"disambiguationData":[OSD([sQuery(id+"F4.wireOp",EDGE,"E5")])],"isStart":true});
            var Q20;
            Q20=makeQuery(id+"F32.opFillet","BLEND_EDGE",EDGE,{"blendedFrom":[makeQuery(id+"F21.boolean.opBoolean","COPY",EDGE,{"derivedFrom":makeQuery(id+"F21.opExtrude","SWEPT_EDGE",EDGE,{"disambiguationData":[OSD([sQuery(id+"F20.wireOp",EDGE,"E32.MirrorCS"),sQuery(id+"F20.wireOp",EDGE,"E35.MirrorCS")])]})}),makeQuery(id+"F5.opExtrude","SWEPT_FACE",FACE,{"disambiguationData":[OSD([sQuery(id+"F4.wireOp",EDGE,"E5")])]})],"blendedInto":[makeQuery(id+"F5.opExtrude","SWEPT_FACE",FACE,{"disambiguationData":[OSD([sQuery(id+"F4.wireOp",EDGE,"E5")])]})]});
            var Q21;
            Q21=makeQuery(id+"F32.opFillet","BLEND_EDGE",EDGE,{"blendedFrom":[makeQuery(id+"F21.boolean.opBoolean","COPY",EDGE,{"derivedFrom":makeQuery(id+"F21.opExtrude","SWEPT_EDGE",EDGE,{"disambiguationData":[OSD([sQuery(id+"F20.wireOp",EDGE,"E28"),sQuery(id+"F20.wireOp",EDGE,"E30")])]})}),makeQuery(id+"F5.opExtrude","SWEPT_FACE",FACE,{"disambiguationData":[OSD([sQuery(id+"F4.wireOp",EDGE,"E5")])]})],"blendedInto":[makeQuery(id+"F5.opExtrude","SWEPT_FACE",FACE,{"disambiguationData":[OSD([sQuery(id+"F4.wireOp",EDGE,"E5")])]})]});
            var Q22;
            Q22=makeQuery(id+"F5.opExtrude","CAP_EDGE",EDGE,{"disambiguationData":[OSD([sQuery(id+"F4.wireOp",EDGE,"E5")])],"isStart":false});
            var Q23;
            Q23=makeQuery(id+"F3.opExtrude","CAP_EDGE",EDGE,{"disambiguationData":[OSD([sQuery(id+"F0.wireOp",EDGE,"E1")])],"isStart":false});
            fillet(context, id + "F33", {"entities" : qUnion([Q0, Q1, Q2, Q3, Q4, Q5, Q6, Q7, Q8, Q9, Q10, Q11, Q12, Q13, Q14, Q15, Q16, Q17, Q18, Q19, Q20, Q21, Q22, Q23]), "radius" : 2 * mm, "tangentPropagation" : true, "allowEdgeOverflow" : false});
        }
        {
            var Q0;
            Q0=makeQuery(id+"F3.boolean.opBoolean","INTERSECT",EDGE,{"derivedFrom":[makeQuery(id+"F2.opExtrude","SWEPT_FACE",FACE,{"disambiguationData":[OSD([sQuery(id+"F1.wireOp",EDGE,"E3")])]}),makeQuery(id+"F3.opExtrude","SWEPT_FACE",FACE,{"disambiguationData":[OSD([sQuery(id+"F0.wireOp",EDGE,"E1")])]})]});
            fillet(context, id + "F34", {"entities" : qUnion([Q0]), "radius" : 3 * mm, "tangentPropagation" : true, "allowEdgeOverflow" : false});
        }
        {
            var Q0;
            Q0=makeQuery(id+"F2.opExtrude","SWEPT_BODY",BODY,{"disambiguationData":[OSD([sQuery(id+"F1.wireOp",EDGE,"E2"),sQuery(id+"F1.wireOp",EDGE,"E3")])]});
            var Q1;
            Q1=qCreatedBy(makeId("Front.planeOp"),FACE);
            mirror(context, id + "F35", {"entities" : qUnion([Q0]), "mirrorPlane" : qUnion([Q1])});
        }
    });
